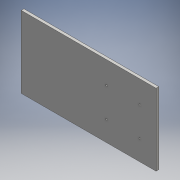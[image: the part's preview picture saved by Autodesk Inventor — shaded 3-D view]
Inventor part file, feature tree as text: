
AUTODESK INVENTOR PART (.ipt)
format: ipt  version: 2016 (Build 200138000, 138)  size: 97,792 bytes
history: native  units: mm
features: extrude x1, sketch x1
ambient origin geometry x8: Origin, YZ Plane, XZ Plane, XY Plane, X Axis, Y Axis, Z Axis, Center Point
bodies: 实体1 (feature_tree)
feature tree (2):
  extrude  "拉伸1"  Depth=80.0mm
  sketch  "草图1"  dims[d0=150.0mm d1=80.0mm d2=18.0mm d3=24.95mm d4=2.0mm d5=32.7mm d6=37.0mm d7=32.7mm d8=2.0mm d9=2.0mm d10=2.0mm d11=3.0mm d12=0.0mm]
